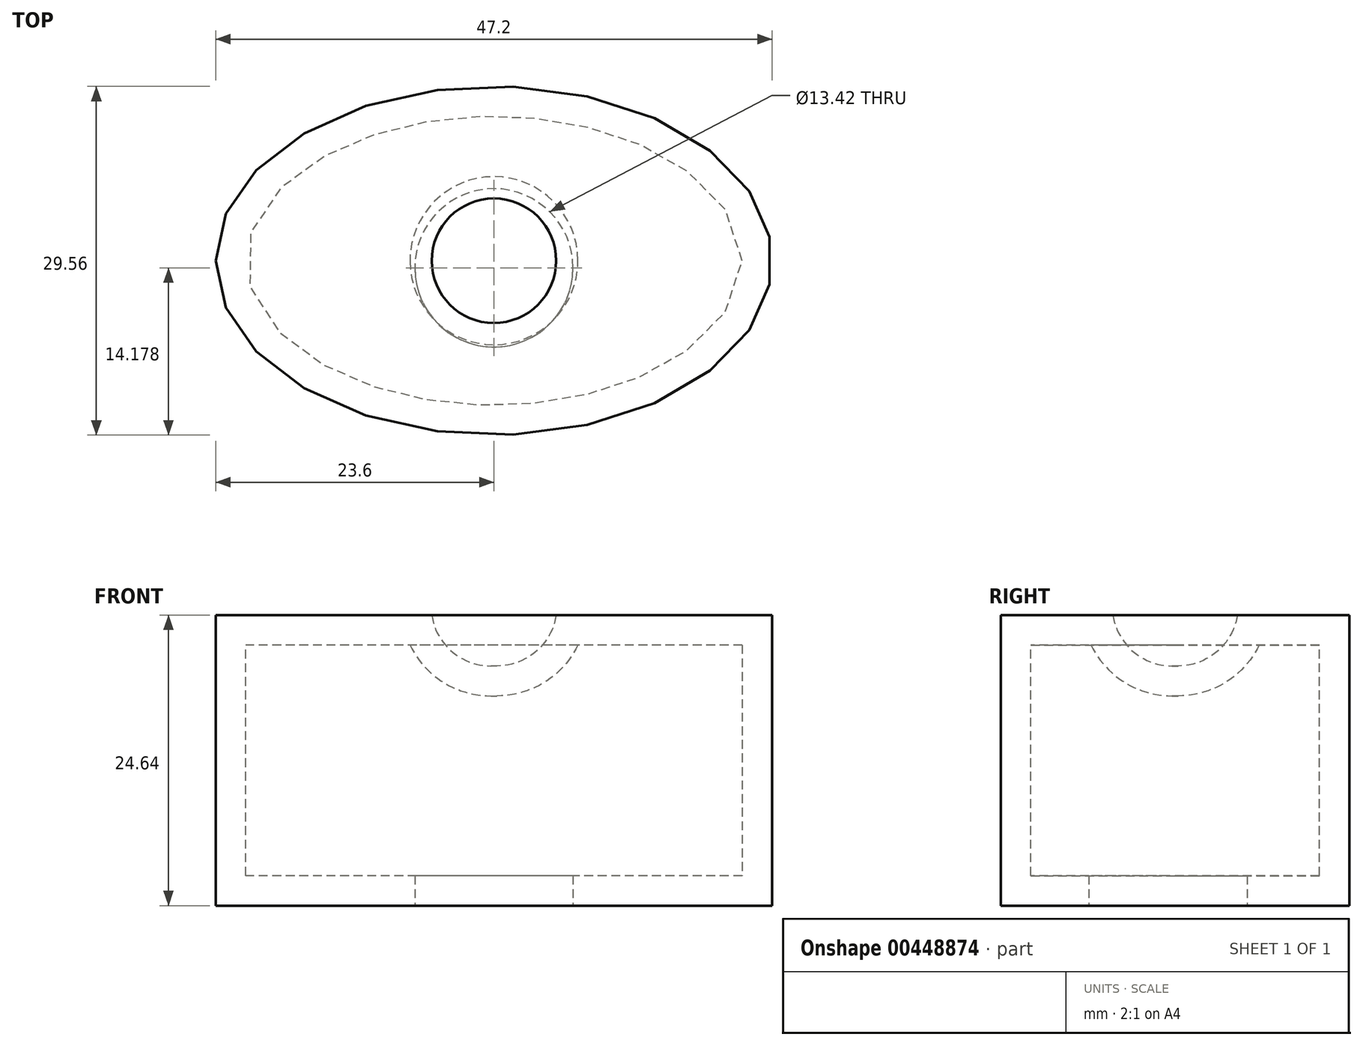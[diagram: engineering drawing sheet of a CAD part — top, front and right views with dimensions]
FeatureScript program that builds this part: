
annotation { "Feature Type Name" : "Feature", "Feature Type Description" : "" }
export const myFeature = defineFeature(function(context is Context, id is Id, definition is map)
    precondition{}
    {
        {
            var Q0;
            Q0=qCreatedBy(makeId("Top.planeOp"),FACE);
            var sketch = newSketch(context, id + "F0", { "sketchPlane" : qUnion([Q0])});
            skEllipse(sketch, "E0", {"center": v(0, 0) * mm, "majorRadius": 23.6 * mm, "minorRadius": 14.78 * mm, "majorAxis": v(-1, 0)});
            skSolve(sketch);
        }
        {
            var Q0;
            Q0=makeQuery(id+"F0.imprint","IMPRINT",FACE,{"disambiguationData":[TD([[makeQuery(id+"F0.imprint","IMPRINT",EDGE,{"derivedFrom":sQuery(id+"F0.wireOp",EDGE,"E0")}),1.0]])]});
            extrude(context, id + "F1", {"entities" : qUnion([Q0]), "depth" : 16 * mm});
        }
        {
            var Q0;
            Q0=makeQuery(id+"F1.opExtrude","CAP_FACE",FACE,{"disambiguationData":[OSD([sQuery(id+"F0.wireOp",EDGE,"E0")])],"isStart":false});
            extrude(context, id + "F2", {"entities" : qUnion([Q0]), "operationType" : NewBodyOperationType.ADD, "depth" : 4.83 * mm});
        }
        {
            var Q0;
            Q0=makeQuery(id+"F2.opExtrude","CAP_FACE",FACE,{"disambiguationData":[OSD([sQuery(id+"F0.wireOp",EDGE,"E0")])],"isStart":false});
            extrude(context, id + "F3", {"entities" : qUnion([Q0]), "operationType" : NewBodyOperationType.ADD, "depth" : 3.8 * mm});
        }
        {
            var Q0;
            Q0=makeQuery(id+"F3.opExtrude","CAP_FACE",FACE,{"disambiguationData":[OSD([sQuery(id+"F0.wireOp",EDGE,"E0")])],"isStart":false});
            var sketch = newSketch(context, id + "F4", { "sketchPlane" : qUnion([Q0])});
            skCircle(sketch, "E1", {"center": v(0, 0) * mm, "radius": 5.28 * mm});
            skSolve(sketch);
        }
        {
            var Q0;
            Q0 = qSketchRegion(id + "F4", true);
            extrude(context, id + "F5", {"entities" : qUnion([Q0]), "operationType" : NewBodyOperationType.REMOVE, "oppositeDirection" : true, "depth" : 4.32 * mm});
        }
        {
            var Q0;
            Q0=makeQuery(id+"F5.boolean.opBoolean","COPY",FACE,{"derivedFrom":makeQuery(id+"F5.opExtrude","CAP_FACE",FACE,{"disambiguationData":[OSD([sQuery(id+"F4.wireOp",EDGE,"E1")])],"isStart":false})});
            fillet(context, id + "F6", {"entities" : qUnion([Q0]), "radius" : 5.08 * mm, "tangentPropagation" : true, "allowEdgeOverflow" : false});
        }
        {
            var Q0;
            Q0=makeQuery(id+"F1.opExtrude","CAP_FACE",FACE,{"disambiguationData":[OSD([sQuery(id+"F0.wireOp",EDGE,"E0")])],"isStart":true});
            var sketch = newSketch(context, id + "F7", { "sketchPlane" : qUnion([Q0])});
            skCircle(sketch, "E2", {"center": v(0, 0.6) * mm, "radius": 6.7 * mm});
            skSolve(sketch);
        }
        {
            var Q0;
            Q0 = qSketchRegion(id + "F7", true);
            extrude(context, id + "F8", {"entities" : qUnion([Q0]), "operationType" : NewBodyOperationType.REMOVE, "oppositeDirection" : true, "depth" : 1.02 * mm});
        }
        {
            var Q0;
            Q0=makeQuery(id+"F8.boolean.opBoolean","COPY",FACE,{"derivedFrom":makeQuery(id+"F8.opExtrude","CAP_FACE",FACE,{"disambiguationData":[OSD([sQuery(id+"F7.wireOp",EDGE,"E2")])],"isStart":false})});
            shell(context, id + "F9", {"entities" : qUnion([Q0]), "thickness" : 2.54 * mm});
        }
        {
            var Q0;
            Q0=makeQuery(id+"F8.boolean.opBoolean","COPY",FACE,{"derivedFrom":makeQuery(id+"F8.opExtrude","CAP_FACE",FACE,{"disambiguationData":[OSD([sQuery(id+"F7.wireOp",EDGE,"E2")])],"isStart":false})});
            extrude(context, id + "F10", {"entities" : qUnion([Q0]), "operationType" : NewBodyOperationType.REMOVE, "oppositeDirection" : true, "depth" : 9.14 * mm});
        }
    });
